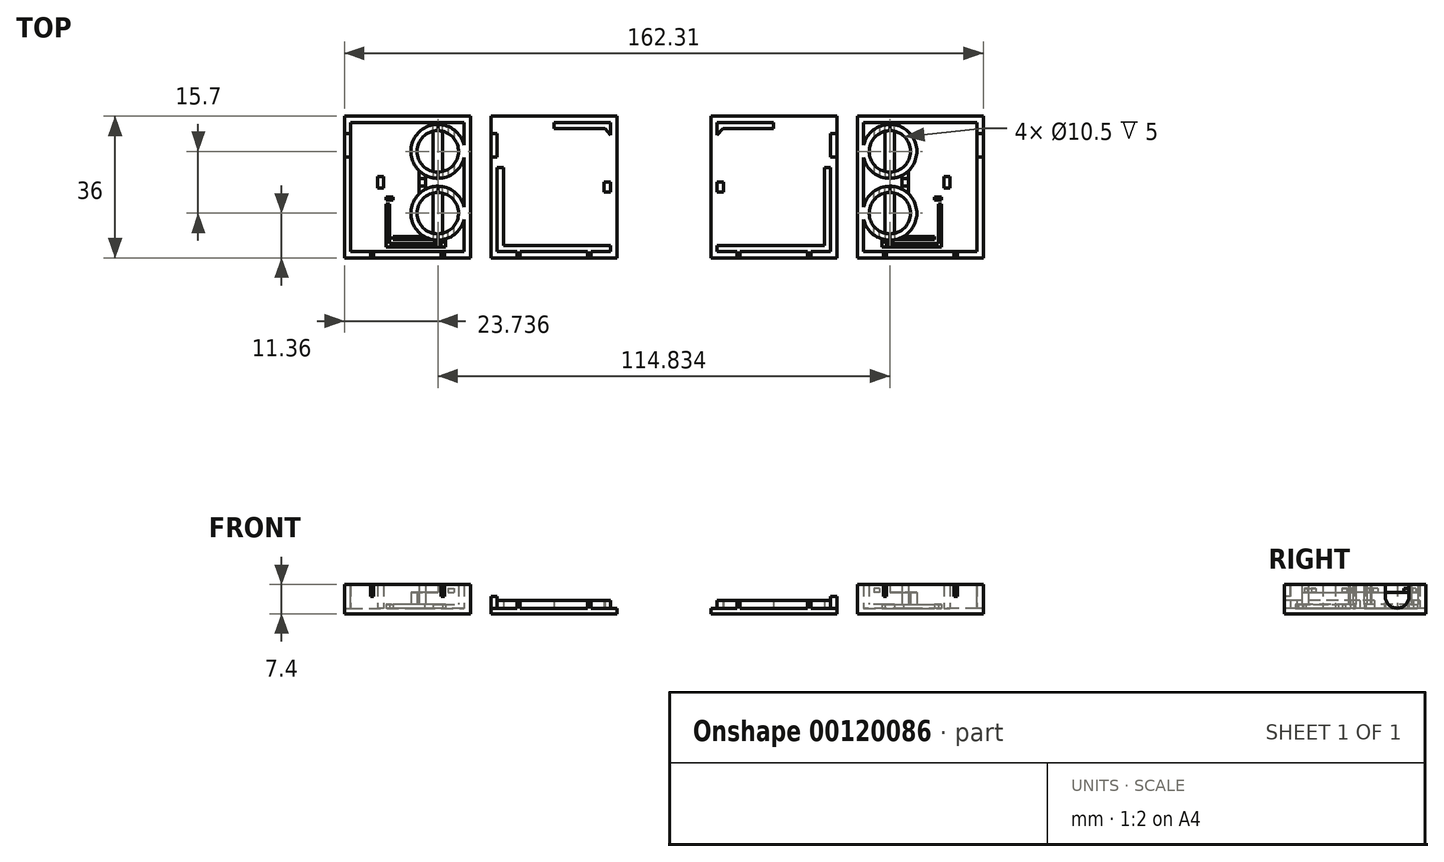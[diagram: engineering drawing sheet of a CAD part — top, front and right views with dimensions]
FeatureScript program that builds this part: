
annotation { "Feature Type Name" : "Feature", "Feature Type Description" : "" }
export const myFeature = defineFeature(function(context is Context, id is Id, definition is map)
    precondition{}
    {
        {
            var Q0;
            Q0=qCreatedBy(makeId("Top.planeOp"),FACE);
            var sketch = newSketch(context, id + "F0", { "sketchPlane" : qUnion([Q0])});
            skLineSegment(sketch, "E0.bottom", {"start": v(-74.61, 24.5) * mm, "end": v(34.71, 24.5) * mm});
            skLineSegment(sketch, "E0.top", {"start": v(-74.61, -26.63) * mm, "end": v(34.71, -26.63) * mm});
            skLineSegment(sketch, "E0.left", {"start": v(-74.61, 24.5) * mm, "end": v(-74.61, -26.63) * mm});
            skLineSegment(sketch, "E0.right", {"start": v(34.71, 24.5) * mm, "end": v(34.71, -26.63) * mm});
            skPoint(sketch, "E1", {"position": v(-57.42, 4.83) * mm});
            skSolve(sketch);
        }
        {
            var Q0;
            Q0=makeQuery(id+"F0.imprint","IMPRINT",FACE,{"disambiguationData":[TD([[makeQuery(id+"F0.imprint","IMPRINT",EDGE,{"derivedFrom":sQuery(id+"F0.wireOp",EDGE,"E0.bottom")}),-1.0]])]});
            extrude(context, id + "F1", {"entities" : qUnion([Q0]), "depth" : 1.4 * mm});
        }
        {
            var Q0;
            Q0=makeQuery(id+"F1.opExtrude","CAP_FACE",FACE,{"disambiguationData":[OSD([sQuery(id+"F0.wireOp",EDGE,"E0.bottom"),sQuery(id+"F0.wireOp",EDGE,"E0.top"),sQuery(id+"F0.wireOp",EDGE,"E0.left"),sQuery(id+"F0.wireOp",EDGE,"E0.right")])],"isStart":false});
            var sketch = newSketch(context, id + "F2", { "sketchPlane" : qUnion([Q0])});
            skPoint(sketch, "E2", {"position": v(0, 12) * mm});
            skCircle(sketch, "E3", {"center": v(0, 12) * mm, "radius": 5.25 * mm});
            skCircle(sketch, "E4", {"center": v(0, 12) * mm, "radius": 6.85 * mm});
            skLineSegment(sketch, "E5", {"start": v(-1.2, 17.11) * mm, "end": v(-1.2, 6.89) * mm});
            skLineSegment(sketch, "E6", {"start": v(-1.2, 17.11) * mm, "end": v(-1.2, 18.74) * mm});
            skLineSegment(sketch, "E7", {"start": v(-1.2, 6.89) * mm, "end": v(-1.2, 5.26) * mm});
            skLineSegment(sketch, "E8", {"start": v(0, -13.27) * mm, "end": v(0, 27.67) * mm, "construction": true});
            skLineSegment(sketch, "E9.MirrorCS", {"start": v(1.2, 17.11) * mm, "end": v(1.2, 18.74) * mm});
            skLineSegment(sketch, "E10.MirrorCS", {"start": v(1.2, 17.11) * mm, "end": v(1.2, 6.89) * mm});
            skLineSegment(sketch, "E11.MirrorCS", {"start": v(1.2, 6.89) * mm, "end": v(1.2, 5.26) * mm});
            skPoint(sketch, "E12", {"position": v(0, -3.7) * mm});
            skCircle(sketch, "E13", {"center": v(0, -3.7) * mm, "radius": 5.25 * mm});
            skCircle(sketch, "E14", {"center": v(0, -3.7) * mm, "radius": 6.85 * mm});
            skLineSegment(sketch, "E15", {"start": v(-1.2, 1.41) * mm, "end": v(-1.2, -8.81) * mm});
            skLineSegment(sketch, "E16", {"start": v(-1.2, 1.41) * mm, "end": v(-1.2, 3.04) * mm});
            skLineSegment(sketch, "E17", {"start": v(-1.2, -8.81) * mm, "end": v(-1.2, -10.44) * mm});
            skLineSegment(sketch, "E18.MirrorCS", {"start": v(1.2, 1.41) * mm, "end": v(1.2, 3.04) * mm});
            skLineSegment(sketch, "E19.MirrorCS", {"start": v(1.2, 1.41) * mm, "end": v(1.2, -8.81) * mm});
            skLineSegment(sketch, "E20.MirrorCS", {"start": v(1.2, -8.81) * mm, "end": v(1.2, -10.44) * mm});
            skPoint(sketch, "E21", {"position": v(0, 5.15) * mm});
            skPoint(sketch, "E22", {"position": v(0, 3.15) * mm});
            skLineSegment(sketch, "E23.bottom", {"start": v(4.73, 7.04) * mm, "end": v(13.73, 7.04) * mm});
            skLineSegment(sketch, "E23.top", {"start": v(4.73, 1.26) * mm, "end": v(13.73, 1.26) * mm});
            skLineSegment(sketch, "E23.left", {"start": v(4.73, 7.04) * mm, "end": v(4.73, 1.26) * mm});
            skLineSegment(sketch, "E23.right", {"start": v(13.73, 7.04) * mm, "end": v(13.73, 1.26) * mm});
            skPoint(sketch, "E24", {"position": v(4.73, 4.15) * mm});
            skPoint(sketch, "E25", {"position": v(0, 4.15) * mm});
            skLineSegment(sketch, "E26", {"start": v(0, 4.15) * mm, "end": v(8.54, 4.15) * mm, "construction": true});
            skLineSegment(sketch, "E27.left", {"start": v(4.73, 6.05) * mm, "end": v(4.73, 2.25) * mm});
            skLineSegment(sketch, "E27.right", {"start": v(3.13, 5.9) * mm, "end": v(3.13, 2.4) * mm});
            skLineSegment(sketch, "E28.bottom", {"start": v(3.13, 5.15) * mm, "end": v(4.73, 5.15) * mm});
            skLineSegment(sketch, "E28.top", {"start": v(3.13, 3.15) * mm, "end": v(4.73, 3.15) * mm});
            skLineSegment(sketch, "E28.left", {"start": v(3.13, 5.15) * mm, "end": v(3.13, 3.15) * mm});
            skLineSegment(sketch, "E28.right", {"start": v(4.73, 5.15) * mm, "end": v(4.73, 3.15) * mm});
            skLineSegment(sketch, "E29.bottom", {"start": v(6.13, 7.04) * mm, "end": v(12.33, 7.04) * mm});
            skLineSegment(sketch, "E29.top", {"start": v(6.13, 7.84) * mm, "end": v(12.33, 7.84) * mm});
            skLineSegment(sketch, "E29.left", {"start": v(6.13, 7.04) * mm, "end": v(6.13, 7.84) * mm});
            skLineSegment(sketch, "E29.right", {"start": v(12.33, 7.04) * mm, "end": v(12.33, 7.84) * mm});
            skLineSegment(sketch, "E30.bottom", {"start": v(13.73, 5.64) * mm, "end": v(15.33, 5.64) * mm});
            skLineSegment(sketch, "E30.top", {"start": v(13.73, 2.66) * mm, "end": v(15.33, 2.66) * mm});
            skLineSegment(sketch, "E30.left", {"start": v(13.73, 5.64) * mm, "end": v(13.73, 2.66) * mm});
            skLineSegment(sketch, "E30.right", {"start": v(15.33, 5.64) * mm, "end": v(15.33, 2.66) * mm});
            skLineSegment(sketch, "E31.bottom", {"start": v(6.13, 1.26) * mm, "end": v(12.33, 1.26) * mm});
            skLineSegment(sketch, "E31.top", {"start": v(6.13, 0.46) * mm, "end": v(12.33, 0.46) * mm});
            skLineSegment(sketch, "E31.left", {"start": v(6.13, 1.26) * mm, "end": v(6.13, 0.46) * mm});
            skLineSegment(sketch, "E31.right", {"start": v(12.33, 1.26) * mm, "end": v(12.33, 0.46) * mm});
            skSolve(sketch);
        }
        {
            var Q0;
            {var subQ0=sQuery(id+"F2.wireOp",EDGE,"E6");Q0=makeQuery(id+"F2.imprint","IMPRINT",FACE,{"disambiguationData":[TD([[makeQuery(id+"F2.imprint","IMPRINT",EDGE,{"derivedFrom":subQ0}),1.0]])]});}
            var Q1;
            {var subQ0=sQuery(id+"F2.wireOp",EDGE,"E6");Q1=makeQuery(id+"F2.imprint","IMPRINT",FACE,{"disambiguationData":[TD([[makeQuery(id+"F2.imprint","IMPRINT",EDGE,{"derivedFrom":subQ0}),-1.0]])]});}
            var Q2;
            {var subQ1=sQuery(id+"F2.wireOp",EDGE,"E9.MirrorCS");Q2=makeQuery(id+"F2.imprint","IMPRINT",FACE,{"disambiguationData":[TD([[makeQuery(id+"F2.imprint","IMPRINT",EDGE,{"derivedFrom":subQ1}),-1.0]])]});}
            var Q3;
            {var subQ0=sQuery(id+"F2.wireOp",EDGE,"E7");Q3=makeQuery(id+"F2.imprint","IMPRINT",FACE,{"disambiguationData":[TD([[makeQuery(id+"F2.imprint","IMPRINT",EDGE,{"derivedFrom":subQ0}),1.0]])]});}
            var Q4;
            {var subQ1=sQuery(id+"F2.wireOp",EDGE,"E18.MirrorCS");Q4=makeQuery(id+"F2.imprint","IMPRINT",FACE,{"disambiguationData":[TD([[makeQuery(id+"F2.imprint","IMPRINT",EDGE,{"derivedFrom":subQ1}),-1.0]])]});}
            var Q5;
            {var subQ0=sQuery(id+"F2.wireOp",EDGE,"E16");Q5=makeQuery(id+"F2.imprint","IMPRINT",FACE,{"disambiguationData":[TD([[makeQuery(id+"F2.imprint","IMPRINT",EDGE,{"derivedFrom":subQ0}),-1.0]])]});}
            var Q6;
            {var subQ0=sQuery(id+"F2.wireOp",EDGE,"E16");Q6=makeQuery(id+"F2.imprint","IMPRINT",FACE,{"disambiguationData":[TD([[makeQuery(id+"F2.imprint","IMPRINT",EDGE,{"derivedFrom":subQ0}),1.0]])]});}
            var Q7;
            {var subQ0=sQuery(id+"F2.wireOp",EDGE,"E17");Q7=makeQuery(id+"F2.imprint","IMPRINT",FACE,{"disambiguationData":[TD([[makeQuery(id+"F2.imprint","IMPRINT",EDGE,{"derivedFrom":subQ0}),1.0]])]});}
            extrude(context, id + "F3", {"entities" : qUnion([Q0, Q1, Q2, Q3, Q4, Q5, Q6, Q7]), "operationType" : NewBodyOperationType.ADD, "depth" : 4 * mm});
        }
        {
            var Q0;
            {var subQ0=sQuery(id+"F2.wireOp",EDGE,"E6");Q0=makeQuery(id+"F2.imprint","IMPRINT",FACE,{"disambiguationData":[TD([[makeQuery(id+"F2.imprint","IMPRINT",EDGE,{"derivedFrom":subQ0}),-1.0]])]});}
            var Q1;
            {var subQ0=sQuery(id+"F2.wireOp",EDGE,"E7");Q1=makeQuery(id+"F2.imprint","IMPRINT",FACE,{"disambiguationData":[TD([[makeQuery(id+"F2.imprint","IMPRINT",EDGE,{"derivedFrom":subQ0}),1.0]])]});}
            var Q2;
            {var subQ0=sQuery(id+"F2.wireOp",EDGE,"E16");Q2=makeQuery(id+"F2.imprint","IMPRINT",FACE,{"disambiguationData":[TD([[makeQuery(id+"F2.imprint","IMPRINT",EDGE,{"derivedFrom":subQ0}),-1.0]])]});}
            var Q3;
            {var subQ0=sQuery(id+"F2.wireOp",EDGE,"E17");Q3=makeQuery(id+"F2.imprint","IMPRINT",FACE,{"disambiguationData":[TD([[makeQuery(id+"F2.imprint","IMPRINT",EDGE,{"derivedFrom":subQ0}),1.0]])]});}
            var Q4;
            {var subQ3=sQuery(id+"F2.wireOp",EDGE,"E28.bottom");Q4=makeQuery(id+"F2.imprint","IMPRINT",FACE,{"disambiguationData":[TD([[makeQuery(id+"F2.imprint","IMPRINT",EDGE,{"derivedFrom":subQ3}),1.0]])]});}
            var Q5;
            {var subQ3=sQuery(id+"F2.wireOp",EDGE,"E28.top");Q5=makeQuery(id+"F2.imprint","IMPRINT",FACE,{"disambiguationData":[TD([[makeQuery(id+"F2.imprint","IMPRINT",EDGE,{"derivedFrom":subQ3}),-1.0]])]});}
            extrude(context, id + "F4", {"entities" : qUnion([Q0, Q1, Q2, Q3, Q4, Q5]), "operationType" : NewBodyOperationType.REMOVE, "depth" : 1 * mm});
        }
        {
            var Q0;
            {var subQ0=sQuery(id+"F2.wireOp",EDGE,"E5");Q0=makeQuery(id+"F2.imprint","IMPRINT",FACE,{"disambiguationData":[TD([[makeQuery(id+"F2.imprint","IMPRINT",EDGE,{"derivedFrom":subQ0}),-1.0]])]});}
            var Q1;
            {var subQ0=sQuery(id+"F2.wireOp",EDGE,"E10.MirrorCS");Q1=makeQuery(id+"F2.imprint","IMPRINT",FACE,{"disambiguationData":[TD([[makeQuery(id+"F2.imprint","IMPRINT",EDGE,{"derivedFrom":subQ0}),1.0]])]});}
            var Q2;
            {var subQ0=sQuery(id+"F2.wireOp",EDGE,"E15");Q2=makeQuery(id+"F2.imprint","IMPRINT",FACE,{"disambiguationData":[TD([[makeQuery(id+"F2.imprint","IMPRINT",EDGE,{"derivedFrom":subQ0}),-1.0]])]});}
            var Q3;
            {var subQ0=sQuery(id+"F2.wireOp",EDGE,"E19.MirrorCS");Q3=makeQuery(id+"F2.imprint","IMPRINT",FACE,{"disambiguationData":[TD([[makeQuery(id+"F2.imprint","IMPRINT",EDGE,{"derivedFrom":subQ0}),1.0]])]});}
            extrude(context, id + "F5", {"entities" : qUnion([Q0, Q1, Q2, Q3]), "operationType" : NewBodyOperationType.ADD, "depth" : 1 * mm});
        }
        {
            var Q0;
            Q0=makeQuery(id+"F3.opExtrude","CAP_FACE",FACE,{"disambiguationData":[OSD([sQuery(id+"F2.wireOp",EDGE,"E3"),sQuery(id+"F2.wireOp",EDGE,"E4")])],"isStart":false});
            var sketch = newSketch(context, id + "F6", { "sketchPlane" : qUnion([Q0])});
            skCircle(sketch, "E32.0", {"center": v(0, 12) * mm, "radius": 6.85 * mm});
            skCircle(sketch, "E32.1", {"center": v(0, 12) * mm, "radius": 5.25 * mm});
            skLineSegment(sketch, "E33", {"start": v(-2.62, 18.33) * mm, "end": v(-2.62, 16.55) * mm});
            skLineSegment(sketch, "E34", {"start": v(-2.62, 7.45) * mm, "end": v(-2.62, 5.67) * mm});
            skLineSegment(sketch, "E35", {"start": v(-4.1, 17.5) * mm, "end": v(-4.1, 15.3) * mm});
            skLineSegment(sketch, "E36", {"start": v(-4.1, 8.7) * mm, "end": v(-4.1, 6.5) * mm});
            skLineSegment(sketch, "E37", {"start": v(0, 18.85) * mm, "end": v(0, 17.25) * mm});
            skLineSegment(sketch, "E38", {"start": v(0, 6.75) * mm, "end": v(0, 5.15) * mm});
            skCircle(sketch, "E39.0", {"center": v(0, -3.7) * mm, "radius": 6.85 * mm});
            skPoint(sketch, "E40", {"position": v(0, 3.15) * mm});
            skPoint(sketch, "E41", {"position": v(0, 5.15) * mm});
            skPoint(sketch, "E42", {"position": v(0, 4.15) * mm});
            skLineSegment(sketch, "E43", {"start": v(0, 4.15) * mm, "end": v(2.8, 4.15) * mm, "construction": true});
            skCircle(sketch, "E44.1", {"center": v(0, -3.7) * mm, "radius": 5.25 * mm});
            skLineSegment(sketch, "E45.MirrorCS", {"start": v(0, -10.55) * mm, "end": v(0, -8.95) * mm});
            skLineSegment(sketch, "E46.MirrorCS", {"start": v(0, 1.55) * mm, "end": v(0, 3.15) * mm});
            skLineSegment(sketch, "E47.MirrorCS", {"start": v(-2.62, 0.85) * mm, "end": v(-2.62, 2.63) * mm});
            skLineSegment(sketch, "E48.MirrorCS", {"start": v(-4.1, -0.4) * mm, "end": v(-4.1, 1.8) * mm});
            skLineSegment(sketch, "E49.MirrorCS", {"start": v(-4.1, -9.2) * mm, "end": v(-4.1, -7) * mm});
            skLineSegment(sketch, "E50.MirrorCS", {"start": v(-2.62, -10.03) * mm, "end": v(-2.62, -8.25) * mm});
            skSolve(sketch);
        }
        {
            var Q0;
            {var subQ0=sQuery(id+"F6.wireOp",EDGE,"E34");Q0=makeQuery(id+"F6.imprint","IMPRINT",FACE,{"disambiguationData":[TD([[makeQuery(id+"F6.imprint","IMPRINT",EDGE,{"derivedFrom":subQ0}),-1.0]])]});}
            var Q1;
            {var subQ0=sQuery(id+"F6.wireOp",EDGE,"E34");Q1=makeQuery(id+"F6.imprint","IMPRINT",FACE,{"disambiguationData":[TD([[makeQuery(id+"F6.imprint","IMPRINT",EDGE,{"derivedFrom":subQ0}),1.0]])]});}
            var Q2;
            {var subQ0=sQuery(id+"F6.wireOp",EDGE,"E35");Q2=makeQuery(id+"F6.imprint","IMPRINT",FACE,{"disambiguationData":[TD([[makeQuery(id+"F6.imprint","IMPRINT",EDGE,{"derivedFrom":subQ0}),-1.0]])]});}
            var Q3;
            {var subQ0=sQuery(id+"F6.wireOp",EDGE,"E33");Q3=makeQuery(id+"F6.imprint","IMPRINT",FACE,{"disambiguationData":[TD([[makeQuery(id+"F6.imprint","IMPRINT",EDGE,{"derivedFrom":subQ0}),-1.0]])]});}
            var Q4;
            {var subQ0=sQuery(id+"F6.wireOp",EDGE,"E33");Q4=makeQuery(id+"F6.imprint","IMPRINT",FACE,{"disambiguationData":[TD([[makeQuery(id+"F6.imprint","IMPRINT",EDGE,{"derivedFrom":subQ0}),1.0]])]});}
            var Q5;
            {var subQ0=sQuery(id+"F6.wireOp",EDGE,"E46.MirrorCS");Q5=makeQuery(id+"F6.imprint","IMPRINT",FACE,{"disambiguationData":[TD([[makeQuery(id+"F6.imprint","IMPRINT",EDGE,{"derivedFrom":subQ0}),1.0]])]});}
            var Q6;
            {var subQ0=sQuery(id+"F6.wireOp",EDGE,"e471a65d-4303-4913-abdb-3468ae2621e10.MirrorCS");Q6=makeQuery(id+"F6.imprint","IMPRINT",FACE,{"disambiguationData":[TD([[makeQuery(id+"F6.imprint","IMPRINT",EDGE,{"derivedFrom":subQ0}),-1.0]])]});}
            var Q7;
            {var subQ0=sQuery(id+"F6.wireOp",EDGE,"5b1a3acc-e78c-430d-9cd8-c20c377ed4240.MirrorCS");Q7=makeQuery(id+"F6.imprint","IMPRINT",FACE,{"disambiguationData":[TD([[makeQuery(id+"F6.imprint","IMPRINT",EDGE,{"derivedFrom":subQ0}),1.0]])]});}
            var Q8;
            {var subQ0=sQuery(id+"F6.wireOp",EDGE,"15c0f35e-76e1-4131-a015-eb208204689e0.MirrorCS");Q8=makeQuery(id+"F6.imprint","IMPRINT",FACE,{"disambiguationData":[TD([[makeQuery(id+"F6.imprint","IMPRINT",EDGE,{"derivedFrom":subQ0}),1.0]])]});}
            var Q9;
            {var subQ0=sQuery(id+"F6.wireOp",EDGE,"E45.MirrorCS");Q9=makeQuery(id+"F6.imprint","IMPRINT",FACE,{"disambiguationData":[TD([[makeQuery(id+"F6.imprint","IMPRINT",EDGE,{"derivedFrom":subQ0}),1.0]])]});}
            var Q10;
            {var subQ0=sQuery(id+"F6.wireOp",EDGE,"E47.MirrorCS");Q10=makeQuery(id+"F6.imprint","IMPRINT",FACE,{"disambiguationData":[TD([[makeQuery(id+"F6.imprint","IMPRINT",EDGE,{"derivedFrom":subQ0}),1.0]])]});}
            var Q11;
            {var subQ0=sQuery(id+"F6.wireOp",EDGE,"E48.MirrorCS");Q11=makeQuery(id+"F6.imprint","IMPRINT",FACE,{"disambiguationData":[TD([[makeQuery(id+"F6.imprint","IMPRINT",EDGE,{"derivedFrom":subQ0}),1.0]])]});}
            var Q12;
            {var subQ0=sQuery(id+"F6.wireOp",EDGE,"E49.MirrorCS");Q12=makeQuery(id+"F6.imprint","IMPRINT",FACE,{"disambiguationData":[TD([[makeQuery(id+"F6.imprint","IMPRINT",EDGE,{"derivedFrom":subQ0}),-1.0]])]});}
            extrude(context, id + "F7", {"entities" : qUnion([Q0, Q1, Q2, Q3, Q4, Q5, Q6, Q7, Q8, Q9, Q10, Q11, Q12]), "operationType" : NewBodyOperationType.ADD, "depth" : 2 * mm});
        }
        {
            var Q0;
            {var subQ0=sQuery(id+"F6.wireOp",EDGE,"E47.MirrorCS");Q0=makeQuery(id+"F6.imprint","IMPRINT",FACE,{"disambiguationData":[TD([[makeQuery(id+"F6.imprint","IMPRINT",EDGE,{"derivedFrom":subQ0}),1.0]])]});}
            var Q1;
            {var subQ0=sQuery(id+"F6.wireOp",EDGE,"E33");Q1=makeQuery(id+"F6.imprint","IMPRINT",FACE,{"disambiguationData":[TD([[makeQuery(id+"F6.imprint","IMPRINT",EDGE,{"derivedFrom":subQ0}),-1.0]])]});}
            var Q2;
            {var subQ0=sQuery(id+"F6.wireOp",EDGE,"E34");Q2=makeQuery(id+"F6.imprint","IMPRINT",FACE,{"disambiguationData":[TD([[makeQuery(id+"F6.imprint","IMPRINT",EDGE,{"derivedFrom":subQ0}),-1.0]])]});}
            var Q3;
            {var subQ0=sQuery(id+"F6.wireOp",EDGE,"E49.MirrorCS");Q3=makeQuery(id+"F6.imprint","IMPRINT",FACE,{"disambiguationData":[TD([[makeQuery(id+"F6.imprint","IMPRINT",EDGE,{"derivedFrom":subQ0}),-1.0]])]});}
            extrude(context, id + "F8", {"entities" : qUnion([Q0, Q1, Q2, Q3]), "operationType" : NewBodyOperationType.REMOVE, "depth" : 1 * mm});
        }
        {
            var Q0;
            Q0=makeQuery(id+"F2.imprint","IMPRINT",FACE,{"disambiguationData":[TD([[makeQuery(id+"F2.imprint","IMPRINT",EDGE,{"derivedFrom":sQuery(id+"F2.wireOp",EDGE,"E28.bottom")}),-1.0]])]});
            extrude(context, id + "F9", {"entities" : qUnion([Q0]), "operationType" : NewBodyOperationType.ADD, "depth" : 4 * mm});
        }
        {
            var Q0;
            {var subQ0=sQuery(id+"F2.wireOp",EDGE,"E27.bottom");Q0=makeQuery(id+"F2.imprint","IMPRINT",FACE,{"disambiguationData":[TD([[makeQuery(id+"F2.imprint","IMPRINT",EDGE,{"derivedFrom":subQ0}),1.0]])]});}
            var Q1;
            {var subQ0=sQuery(id+"F2.wireOp",EDGE,"E27.top");Q1=makeQuery(id+"F2.imprint","IMPRINT",FACE,{"disambiguationData":[TD([[makeQuery(id+"F2.imprint","IMPRINT",EDGE,{"derivedFrom":subQ0}),-1.0]])]});}
            var Q2;
            Q2=makeQuery(id+"F2.imprint","IMPRINT",FACE,{"disambiguationData":[TD([[makeQuery(id+"F2.imprint","IMPRINT",EDGE,{"derivedFrom":sQuery(id+"F2.wireOp",EDGE,"E29.bottom")}),1.0]])]});
            var Q3;
            Q3=makeQuery(id+"F2.imprint","IMPRINT",FACE,{"disambiguationData":[TD([[makeQuery(id+"F2.imprint","IMPRINT",EDGE,{"derivedFrom":sQuery(id+"F2.wireOp",EDGE,"E30.bottom")}),-1.0]])]});
            var Q4;
            Q4=makeQuery(id+"F2.imprint","IMPRINT",FACE,{"disambiguationData":[TD([[makeQuery(id+"F2.imprint","IMPRINT",EDGE,{"derivedFrom":sQuery(id+"F2.wireOp",EDGE,"E31.bottom")}),-1.0]])]});
            var Q5;
            {var subQ3=sQuery(id+"F2.wireOp",EDGE,"E28.bottom");Q5=makeQuery(id+"F2.imprint","IMPRINT",FACE,{"disambiguationData":[TD([[makeQuery(id+"F2.imprint","IMPRINT",EDGE,{"derivedFrom":subQ3}),1.0]])]});}
            var Q6;
            {var subQ3=sQuery(id+"F2.wireOp",EDGE,"E28.top");Q6=makeQuery(id+"F2.imprint","IMPRINT",FACE,{"disambiguationData":[TD([[makeQuery(id+"F2.imprint","IMPRINT",EDGE,{"derivedFrom":subQ3}),-1.0]])]});}
            extrude(context, id + "F10", {"entities" : qUnion([Q0, Q1, Q2, Q3, Q4, Q5, Q6]), "operationType" : NewBodyOperationType.ADD, "depth" : 6 * mm});
        }
        {
            var Q0;
            {var subQ0=sQuery(id+"F2.wireOp",EDGE,"E14");var subQ1=sQuery(id+"F2.wireOp",EDGE,"E13");var subQ2=sQuery(id+"F2.wireOp",EDGE,"E4");var subQ3=sQuery(id+"F2.wireOp",EDGE,"E3");var subQ4=sQuery(id+"F0.wireOp",EDGE,"E0.right");var subQ5=sQuery(id+"F0.wireOp",EDGE,"E0.left");var subQ6=sQuery(id+"F0.wireOp",EDGE,"E0.top");var subQ7=sQuery(id+"F0.wireOp",EDGE,"E0.bottom");var subQ8=makeQuery(id+"F1.opExtrude","CAP_FACE",FACE,{"disambiguationData":[OSD([subQ7,subQ6,subQ5,subQ4])],"isStart":false});Q0=makeQuery(id+"F4.boolean.opBoolean","MERGE",FACE,{"derivedFrom":[makeQuery(id+"F3.boolean.opBoolean","SPLIT",FACE,{"disambiguationData":[TD([makeQuery(id+"F1.opExtrude","SWEPT_FACE",FACE,{"disambiguationData":[OSD([subQ7])]})])],"derivedFrom":subQ8}),makeQuery(id+"F3.boolean.opBoolean","SPLIT",FACE,{"disambiguationData":[TD([makeQuery(id+"F3.opExtrude","SWEPT_FACE",FACE,{"disambiguationData":[OSD([subQ3])]})])],"derivedFrom":subQ8}),makeQuery(id+"F3.boolean.opBoolean","SPLIT",FACE,{"disambiguationData":[TD([makeQuery(id+"F3.opExtrude","SWEPT_FACE",FACE,{"disambiguationData":[OSD([subQ1])]})])],"derivedFrom":subQ8}),makeQuery(id+"F4.opExtrude","CAP_FACE",FACE,{"disambiguationData":[OSD([subQ3,subQ2,sQuery(id+"F2.wireOp",EDGE,"E6"),sQuery(id+"F2.wireOp",EDGE,"E9.MirrorCS")])],"isStart":true}),makeQuery(id+"F4.opExtrude","CAP_FACE",FACE,{"disambiguationData":[OSD([subQ3,subQ2,sQuery(id+"F2.wireOp",EDGE,"E7"),sQuery(id+"F2.wireOp",EDGE,"E11.MirrorCS")])],"isStart":true}),makeQuery(id+"F4.opExtrude","CAP_FACE",FACE,{"disambiguationData":[OSD([subQ1,subQ0,sQuery(id+"F2.wireOp",EDGE,"E16"),sQuery(id+"F2.wireOp",EDGE,"E18.MirrorCS")])],"isStart":true}),makeQuery(id+"F4.opExtrude","CAP_FACE",FACE,{"disambiguationData":[OSD([subQ1,subQ0,sQuery(id+"F2.wireOp",EDGE,"E17"),sQuery(id+"F2.wireOp",EDGE,"E20.MirrorCS")])],"isStart":true})]});}
            var sketch = newSketch(context, id + "F11", { "sketchPlane" : qUnion([Q0])});
            skCircle(sketch, "E51.0", {"center": v(0, -3.7) * mm, "radius": 6.85 * mm});
            skLineSegment(sketch, "E52.bottom", {"start": v(-1.2, -10.44) * mm, "end": v(12.33, -10.44) * mm});
            skLineSegment(sketch, "E52.top", {"start": v(-1.2, -11.44) * mm, "end": v(12.33, -11.44) * mm});
            skLineSegment(sketch, "E52.left", {"start": v(-1.2, -10.44) * mm, "end": v(-1.2, -11.44) * mm});
            skLineSegment(sketch, "E52.right", {"start": v(12.33, -10.44) * mm, "end": v(12.33, -11.44) * mm});
            skLineSegment(sketch, "E53.bottom", {"start": v(12.33, -10.44) * mm, "end": v(11.33, -10.44) * mm});
            skLineSegment(sketch, "E53.top", {"start": v(12.33, 0.46) * mm, "end": v(11.33, 0.46) * mm});
            skLineSegment(sketch, "E53.left", {"start": v(12.33, -10.44) * mm, "end": v(12.33, 0.46) * mm});
            skLineSegment(sketch, "E53.right", {"start": v(11.33, -10.44) * mm, "end": v(11.33, 0.46) * mm});
            skLineSegment(sketch, "E54.bottom", {"start": v(11.33, -1.34) * mm, "end": v(22.04, -1.34) * mm});
            skLineSegment(sketch, "E54.top", {"start": v(11.33, -0.34) * mm, "end": v(22.04, -0.34) * mm});
            skLineSegment(sketch, "E54.left", {"start": v(11.33, -1.34) * mm, "end": v(11.33, -0.34) * mm});
            skLineSegment(sketch, "E54.right", {"start": v(22.04, -1.34) * mm, "end": v(22.04, -0.34) * mm});
            skPoint(sketch, "E55", {"position": v(12.33, -0.34) * mm});
            skPoint(sketch, "E56", {"position": v(12.33, -1.34) * mm});
            skLineSegment(sketch, "E57.bottom", {"start": v(-2, -9.64) * mm, "end": v(13.13, -9.64) * mm});
            skLineSegment(sketch, "E57.top", {"start": v(-2, -12.24) * mm, "end": v(13.13, -12.24) * mm});
            skLineSegment(sketch, "E57.left", {"start": v(-2, -9.64) * mm, "end": v(-2, -12.24) * mm});
            skLineSegment(sketch, "E57.right", {"start": v(13.13, -9.64) * mm, "end": v(13.13, -12.24) * mm});
            skLineSegment(sketch, "E58.bottom", {"start": v(13.13, -9.64) * mm, "end": v(10.53, -9.64) * mm});
            skLineSegment(sketch, "E58.top", {"start": v(13.13, 0.46) * mm, "end": v(10.53, 0.46) * mm});
            skLineSegment(sketch, "E58.left", {"start": v(13.13, -9.64) * mm, "end": v(13.13, 0.46) * mm});
            skLineSegment(sketch, "E58.right", {"start": v(10.53, -9.64) * mm, "end": v(10.53, 0.46) * mm});
            skLineSegment(sketch, "E59.bottom", {"start": v(13.13, 0.46) * mm, "end": v(21.62, 0.46) * mm});
            skLineSegment(sketch, "E59.top", {"start": v(13.13, -2.14) * mm, "end": v(21.62, -2.14) * mm});
            skLineSegment(sketch, "E59.left", {"start": v(13.13, 0.46) * mm, "end": v(13.13, -2.14) * mm});
            skLineSegment(sketch, "E59.right", {"start": v(21.62, 0.46) * mm, "end": v(21.62, -2.14) * mm});
            skPoint(sketch, "E60", {"position": v(3.4, -9.64) * mm});
            skPoint(sketch, "E61", {"position": v(-2, -10.25) * mm});
            skPoint(sketch, "E62", {"position": v(-1.2, -10.44) * mm});
            skLineSegment(sketch, "E63.bottom", {"start": v(6.8, 19.34) * mm, "end": v(22.14, 19.34) * mm});
            skLineSegment(sketch, "E63.top", {"start": v(6.8, 7.84) * mm, "end": v(22.14, 7.84) * mm});
            skLineSegment(sketch, "E63.left", {"start": v(6.8, 11.2) * mm, "end": v(6.8, 7.84) * mm});
            skLineSegment(sketch, "E63.right", {"start": v(22.14, 19.34) * mm, "end": v(22.14, 7.84) * mm});
            skLineSegment(sketch, "E64", {"start": v(6.8, 19.34) * mm, "end": v(6.8, 11.2) * mm});
            skLineSegment(sketch, "E65", {"start": v(22.14, 7.84) * mm, "end": v(22.14, -11.25) * mm});
            skLineSegment(sketch, "E66.bottom", {"start": v(22.14, 19.34) * mm, "end": v(-6.66, 19.34) * mm});
            skLineSegment(sketch, "E66.top", {"start": v(22.14, -13.46) * mm, "end": v(-6.66, -13.46) * mm});
            skLineSegment(sketch, "E66.left", {"start": v(22.14, 19.34) * mm, "end": v(22.14, -13.46) * mm});
            skLineSegment(sketch, "E66.right", {"start": v(-6.66, 19.34) * mm, "end": v(-6.66, -13.46) * mm});
            skLineSegment(sketch, "E67.bottom", {"start": v(23.74, -15.06) * mm, "end": v(-8.26, -15.06) * mm});
            skLineSegment(sketch, "E67.top", {"start": v(23.74, 20.94) * mm, "end": v(-8.26, 20.94) * mm});
            skLineSegment(sketch, "E67.left", {"start": v(23.74, -15.06) * mm, "end": v(23.74, 20.94) * mm});
            skLineSegment(sketch, "E67.right", {"start": v(-8.26, -15.06) * mm, "end": v(-8.26, 20.94) * mm});
            skLineSegment(sketch, "E68.bottom", {"start": v(-13.46, 20.94) * mm, "end": v(-45.46, 20.94) * mm});
            skLineSegment(sketch, "E68.top", {"start": v(-13.46, -15.06) * mm, "end": v(-45.46, -15.06) * mm});
            skLineSegment(sketch, "E68.left", {"start": v(-13.46, 20.94) * mm, "end": v(-13.46, -15.06) * mm});
            skLineSegment(sketch, "E68.right", {"start": v(-45.46, 20.94) * mm, "end": v(-45.46, -15.06) * mm});
            skLineSegment(sketch, "E69.bottom", {"start": v(-43.86, 19.34) * mm, "end": v(-15.06, 19.34) * mm});
            skLineSegment(sketch, "E69.top", {"start": v(-43.86, -13.46) * mm, "end": v(-15.06, -13.46) * mm});
            skLineSegment(sketch, "E69.left", {"start": v(-43.86, 19.34) * mm, "end": v(-43.86, -13.46) * mm});
            skLineSegment(sketch, "E69.right", {"start": v(-15.06, 19.34) * mm, "end": v(-15.06, -13.46) * mm});
            skLineSegment(sketch, "E70", {"start": v(-43.86, 16.14) * mm, "end": v(-41.03, 19.34) * mm});
            skPoint(sketch, "E71.firstSnap0", {"position": v(3.13, 4.15) * mm});
            skLineSegment(sketch, "E71.bottom", {"start": v(-43.86, 4.15) * mm, "end": v(-42.26, 4.15) * mm});
            skLineSegment(sketch, "E71.top", {"start": v(-43.86, 1.65) * mm, "end": v(-42.26, 1.65) * mm});
            skLineSegment(sketch, "E71.left", {"start": v(-43.86, 4.15) * mm, "end": v(-43.86, 1.65) * mm});
            skLineSegment(sketch, "E71.right", {"start": v(-42.26, 4.15) * mm, "end": v(-42.26, 1.65) * mm});
            skLineSegment(sketch, "E72.bottom", {"start": v(-42.26, 4.15) * mm, "end": v(-43.86, 4.15) * mm});
            skLineSegment(sketch, "E72.top", {"start": v(-42.26, 6.65) * mm, "end": v(-43.86, 6.65) * mm});
            skLineSegment(sketch, "E72.left", {"start": v(-42.26, 4.15) * mm, "end": v(-42.26, 6.65) * mm});
            skLineSegment(sketch, "E72.right", {"start": v(-43.86, 4.15) * mm, "end": v(-43.86, 6.65) * mm});
            skLineSegment(sketch, "E73", {"start": v(-43.86, -11.86) * mm, "end": v(-15.06, -11.86) * mm});
            skPoint(sketch, "E74", {"position": v(-15.06, 7.84) * mm});
            skLineSegment(sketch, "E75.bottom", {"start": v(-15.06, 7.84) * mm, "end": v(-16.66, 7.84) * mm});
            skLineSegment(sketch, "E75.top", {"start": v(-15.06, -11.86) * mm, "end": v(-16.66, -11.86) * mm});
            skLineSegment(sketch, "E75.left", {"start": v(-15.06, 7.84) * mm, "end": v(-15.06, -11.86) * mm});
            skLineSegment(sketch, "E75.right", {"start": v(-16.66, 7.84) * mm, "end": v(-16.66, -11.86) * mm});
            skPoint(sketch, "E76", {"position": v(-15.06, 19.34) * mm});
            skPoint(sketch, "E77", {"position": v(-29.56, 19.34) * mm});
            skLineSegment(sketch, "E78.bottom", {"start": v(-29.56, 19.34) * mm, "end": v(-42.45, 19.34) * mm});
            skLineSegment(sketch, "E78.top", {"start": v(-29.56, 17.74) * mm, "end": v(-42.45, 17.74) * mm});
            skLineSegment(sketch, "E78.left", {"start": v(-29.56, 19.34) * mm, "end": v(-29.56, 17.74) * mm});
            skLineSegment(sketch, "E78.right", {"start": v(-42.45, 19.34) * mm, "end": v(-42.45, 17.74) * mm});
            skPoint(sketch, "E79", {"position": v(-38.86, -13.46) * mm});
            skPoint(sketch, "E80", {"position": v(-38.06, -13.46) * mm});
            skPoint(sketch, "E81", {"position": v(-20.06, -13.46) * mm});
            skPoint(sketch, "E82", {"position": v(-20.86, -13.46) * mm});
            skLineSegment(sketch, "E83", {"start": v(-38.86, -13.46) * mm, "end": v(-38.86, -15.06) * mm});
            skLineSegment(sketch, "E84", {"start": v(-38.06, -13.46) * mm, "end": v(-38.06, -15.06) * mm});
            skLineSegment(sketch, "E85", {"start": v(-20.86, -13.46) * mm, "end": v(-20.86, -15.06) * mm});
            skLineSegment(sketch, "E86", {"start": v(-20.06, -13.46) * mm, "end": v(-20.06, -15.06) * mm});
            skPoint(sketch, "E87", {"position": v(-15.06, 13.6) * mm});
            skLineSegment(sketch, "E88", {"start": v(-15.06, 16.6) * mm, "end": v(-13.46, 16.6) * mm});
            skLineSegment(sketch, "E89", {"start": v(-15.06, 10.6) * mm, "end": v(-13.46, 10.6) * mm});
            skPoint(sketch, "E90.0", {"position": v(1.2, -10.44) * mm});
            skSolve(sketch);
        }
        {
            var Q0;
            {var subQ1=sQuery(id+"F11.wireOp",EDGE,"E52.bottom");var subQ7=sQuery(id+"F11.wireOp",EDGE,"E51.0");var subQ9=makeQuery(id+"F11.imprint","INTERSECT",VERTEX,{"derivedFrom":[subQ7,subQ1]});Q0=makeQuery(id+"F11.imprint","IMPRINT",FACE,{"disambiguationData":[TD([[makeQuery(id+"F11.imprint","IMPRINT",EDGE,{"disambiguationData":[TD([[subQ9,-1.0]])],"derivedFrom":subQ7}),-1.0]])]});}
            var Q1;
            {var subQ4=sQuery(id+"F11.wireOp",EDGE,"E54.left");Q1=makeQuery(id+"F11.imprint","IMPRINT",FACE,{"disambiguationData":[TD([[makeQuery(id+"F11.imprint","IMPRINT",EDGE,{"derivedFrom":subQ4}),1.0]])]});}
            var Q2;
            {var subQ0=sQuery(id+"F11.wireOp",EDGE,"E58.left");Q2=makeQuery(id+"F11.imprint","IMPRINT",FACE,{"disambiguationData":[TD([[makeQuery(id+"F11.imprint","IMPRINT",EDGE,{"derivedFrom":subQ0}),1.0]])]});}
            var Q3;
            {var subQ0=sQuery(id+"F11.wireOp",EDGE,"E58.top");var subQ1=sQuery(id+"F11.wireOp",EDGE,"E53.left");var subQ2=makeQuery(id+"F11.imprint","INTERSECT",VERTEX,{"derivedFrom":[subQ1,subQ0]});Q3=makeQuery(id+"F11.imprint","IMPRINT",FACE,{"disambiguationData":[TD([[makeQuery(id+"F11.imprint","IMPRINT",EDGE,{"disambiguationData":[TD([[subQ2,1.0]])],"derivedFrom":subQ1}),-1.0]])]});}
            var Q4;
            {var subQ0=sQuery(id+"F11.wireOp",EDGE,"E58.top");var subQ1=sQuery(id+"F11.wireOp",EDGE,"E53.left");var subQ2=makeQuery(id+"F11.imprint","INTERSECT",VERTEX,{"derivedFrom":[subQ1,subQ0]});Q4=makeQuery(id+"F11.imprint","IMPRINT",FACE,{"disambiguationData":[TD([[makeQuery(id+"F11.imprint","IMPRINT",EDGE,{"disambiguationData":[TD([[subQ2,1.0]])],"derivedFrom":subQ1}),1.0]])]});}
            var Q5;
            {var subQ5=sQuery(id+"F11.wireOp",EDGE,"E52.top");Q5=makeQuery(id+"F11.imprint","IMPRINT",FACE,{"disambiguationData":[TD([[makeQuery(id+"F11.imprint","IMPRINT",EDGE,{"derivedFrom":subQ5}),-1.0]])]});}
            extrude(context, id + "F12", {"entities" : qUnion([Q0, Q1, Q2, Q3, Q4, Q5]), "operationType" : NewBodyOperationType.ADD, "depth" : 1 * mm});
        }
        {
            var Q0;
            {var subQ2=sQuery(id+"F11.wireOp",EDGE,"E66.top");Q0=makeQuery(id+"F11.imprint","IMPRINT",FACE,{"disambiguationData":[TD([[makeQuery(id+"F11.imprint","IMPRINT",EDGE,{"derivedFrom":subQ2}),1.0]])]});}
            extrude(context, id + "F13", {"entities" : qUnion([Q0]), "operationType" : NewBodyOperationType.ADD, "depth" : 6 * mm});
        }
        {
            var Q0;
            Q0=makeQuery(id+"F13.opExtrude","SWEPT_FACE",FACE,{"disambiguationData":[OSD([sQuery(id+"F11.wireOp",EDGE,"E66.left")])]});
            var sketch = newSketch(context, id + "F14", { "sketchPlane" : qUnion([Q0])});
            skPoint(sketch, "E91.0", {"position": v(-7.84, 1.4) * mm});
            skPoint(sketch, "E91.1", {"position": v(-19.34, 1.4) * mm});
            skLineSegment(sketch, "E92.1", {"start": v(-19.34, 1.4) * mm, "end": v(13.46, 1.4) * mm});
            skPoint(sketch, "E93", {"position": v(-13.6, 1.4) * mm});
            skLineSegment(sketch, "E94", {"start": v(-13.6, 1.4) * mm, "end": v(-13.6, 7.4) * mm});
            skPoint(sketch, "E95", {"position": v(-13.6, 4.4) * mm});
            skCircle(sketch, "E96", {"center": v(-13.6, 4.4) * mm, "radius": 3 * mm});
            skLineSegment(sketch, "E97", {"start": v(-16.6, 4.4) * mm, "end": v(-16.6, 7.4) * mm});
            skLineSegment(sketch, "E98", {"start": v(-10.6, 4.4) * mm, "end": v(-10.6, 7.4) * mm});
            skSolve(sketch);
        }
        {
            var Q0;
            {var subQ3=sQuery(id+"F14.wireOp",EDGE,"E97");Q0=makeQuery(id+"F14.imprint","IMPRINT",FACE,{"disambiguationData":[TD([[makeQuery(id+"F14.imprint","IMPRINT",EDGE,{"derivedFrom":subQ3}),-1.0]])]});}
            var Q1;
            {var subQ0=sQuery(id+"F14.wireOp",EDGE,"E94");Q1=makeQuery(id+"F14.imprint","IMPRINT",FACE,{"disambiguationData":[TD([[makeQuery(id+"F14.imprint","IMPRINT",EDGE,{"derivedFrom":subQ0}),1.0]])]});}
            var Q2;
            {var subQ0=sQuery(id+"F14.wireOp",EDGE,"E94");Q2=makeQuery(id+"F14.imprint","IMPRINT",FACE,{"disambiguationData":[TD([[makeQuery(id+"F14.imprint","IMPRINT",EDGE,{"derivedFrom":subQ0}),-1.0]])]});}
            var Q3;
            {var subQ3=sQuery(id+"F14.wireOp",EDGE,"E98");Q3=makeQuery(id+"F14.imprint","IMPRINT",FACE,{"disambiguationData":[TD([[makeQuery(id+"F14.imprint","IMPRINT",EDGE,{"derivedFrom":subQ3}),1.0]])]});}
            extrude(context, id + "F15", {"entities" : qUnion([Q0, Q1, Q2, Q3]), "operationType" : NewBodyOperationType.REMOVE, "oppositeDirection" : true, "depth" : 2 * mm});
        }
        {
            var Q0;
            Q0=makeQuery(id+"F13.opExtrude","CAP_FACE",FACE,{"disambiguationData":[OSD([sQuery(id+"F11.wireOp",EDGE,"E66.bottom"),sQuery(id+"F11.wireOp",EDGE,"E66.top"),sQuery(id+"F11.wireOp",EDGE,"E66.left"),sQuery(id+"F11.wireOp",EDGE,"E66.right"),sQuery(id+"F11.wireOp",EDGE,"E67.bottom"),sQuery(id+"F11.wireOp",EDGE,"E67.top"),sQuery(id+"F11.wireOp",EDGE,"E67.left"),sQuery(id+"F11.wireOp",EDGE,"E67.right")])],"isStart":false});
            var sketch = newSketch(context, id + "F16", { "sketchPlane" : qUnion([Q0])});
            skPoint(sketch, "E99", {"position": v(-1.66, -13.46) * mm});
            skPoint(sketch, "E100", {"position": v(-0.86, -13.46) * mm});
            skPoint(sketch, "E101", {"position": v(17.14, -13.46) * mm});
            skPoint(sketch, "E102", {"position": v(16.34, -13.46) * mm});
            skLineSegment(sketch, "E103", {"start": v(-1.66, -13.46) * mm, "end": v(-1.66, -15.06) * mm});
            skLineSegment(sketch, "E104", {"start": v(-0.86, -13.46) * mm, "end": v(-0.86, -15.06) * mm});
            skLineSegment(sketch, "E105", {"start": v(16.34, -13.46) * mm, "end": v(16.34, -15.06) * mm});
            skLineSegment(sketch, "E106", {"start": v(17.14, -13.46) * mm, "end": v(17.14, -15.06) * mm});
            skSolve(sketch);
        }
        {
            var Q0;
            {var subQ0=sQuery(id+"F16.wireOp",EDGE,"E103");Q0=makeQuery(id+"F16.imprint","IMPRINT",FACE,{"disambiguationData":[TD([[makeQuery(id+"F16.imprint","IMPRINT",EDGE,{"derivedFrom":subQ0}),1.0]])]});}
            var Q1;
            {var subQ5=sQuery(id+"F16.wireOp",EDGE,"E106");Q1=makeQuery(id+"F16.imprint","IMPRINT",FACE,{"disambiguationData":[TD([[makeQuery(id+"F16.imprint","IMPRINT",EDGE,{"derivedFrom":subQ5}),-1.0]])]});}
            extrude(context, id + "F17", {"entities" : qUnion([Q0, Q1]), "operationType" : NewBodyOperationType.REMOVE, "oppositeDirection" : true, "depth" : 3 * mm});
        }
        {
            var Q0;
            {var subQ0=sQuery(id+"F11.wireOp",EDGE,"E88");Q0=makeQuery(id+"F11.imprint","IMPRINT",FACE,{"disambiguationData":[TD([[makeQuery(id+"F11.imprint","IMPRINT",EDGE,{"derivedFrom":subQ0}),-1.0]])]});}
            extrude(context, id + "F18", {"entities" : qUnion([Q0]), "operationType" : NewBodyOperationType.ADD, "depth" : 3 * mm});
        }
        {
            var Q0;
            Q0=makeQuery(id+"F18.opExtrude","SWEPT_FACE",FACE,{"disambiguationData":[OSD([sQuery(id+"F11.wireOp",EDGE,"E69.right")])]});
            var sketch = newSketch(context, id + "F19", { "sketchPlane" : qUnion([Q0])});
            skPoint(sketch, "E107", {"position": v(-13.6, 4.4) * mm});
            skCircle(sketch, "E108", {"center": v(-13.6, 4.4) * mm, "radius": 3 * mm});
            skSolve(sketch);
        }
        {
            var Q0;
            Q0 = qSketchRegion(id + "F19", true);
            extrude(context, id + "F20", {"entities" : qUnion([Q0]), "operationType" : NewBodyOperationType.REMOVE, "oppositeDirection" : true, "depth" : 2 * mm});
        }
        {
            var Q0;
            Q0=makeQuery(id+"F11.imprint","IMPRINT",FACE,{"disambiguationData":[TD([[makeQuery(id+"F11.imprint","IMPRINT",EDGE,{"derivedFrom":sQuery(id+"F11.wireOp",EDGE,"E75.bottom")}),1.0]])]});
            var Q1;
            {var subQ3=sQuery(id+"F11.wireOp",EDGE,"E78.top");Q1=makeQuery(id+"F11.imprint","IMPRINT",FACE,{"disambiguationData":[TD([[makeQuery(id+"F11.imprint","IMPRINT",EDGE,{"derivedFrom":subQ3}),-1.0]])]});}
            var Q2;
            {var subQ9=sQuery(id+"F11.wireOp",EDGE,"E73");Q2=makeQuery(id+"F11.imprint","IMPRINT",FACE,{"disambiguationData":[TD([[makeQuery(id+"F11.imprint","IMPRINT",EDGE,{"derivedFrom":subQ9}),-1.0]])]});}
            var Q3;
            {var subQ3=sQuery(id+"F11.wireOp",EDGE,"E78.right");Q3=makeQuery(id+"F11.imprint","IMPRINT",FACE,{"disambiguationData":[TD([[makeQuery(id+"F11.imprint","IMPRINT",EDGE,{"derivedFrom":subQ3}),-1.0]])]});}
            var Q4;
            {var subQ3=sQuery(id+"F11.wireOp",EDGE,"E78.right");Q4=makeQuery(id+"F11.imprint","IMPRINT",FACE,{"disambiguationData":[TD([[makeQuery(id+"F11.imprint","IMPRINT",EDGE,{"derivedFrom":subQ3}),1.0]])]});}
            var Q5;
            Q5=makeQuery(id+"F11.imprint","IMPRINT",FACE,{"disambiguationData":[TD([[makeQuery(id+"F11.imprint","IMPRINT",EDGE,{"derivedFrom":sQuery(id+"F11.wireOp",EDGE,"E72.bottom")}),-1.0]])]});
            var Q6;
            Q6=makeQuery(id+"F11.imprint","IMPRINT",FACE,{"disambiguationData":[TD([[makeQuery(id+"F11.imprint","IMPRINT",EDGE,{"derivedFrom":sQuery(id+"F11.wireOp",EDGE,"E71.top")}),1.0]])]});
            var Q7;
            {var subQ0=sQuery(id+"F11.wireOp",EDGE,"E83");Q7=makeQuery(id+"F11.imprint","IMPRINT",FACE,{"disambiguationData":[TD([[makeQuery(id+"F11.imprint","IMPRINT",EDGE,{"derivedFrom":subQ0}),1.0]])]});}
            var Q8;
            {var subQ0=sQuery(id+"F11.wireOp",EDGE,"E85");Q8=makeQuery(id+"F11.imprint","IMPRINT",FACE,{"disambiguationData":[TD([[makeQuery(id+"F11.imprint","IMPRINT",EDGE,{"derivedFrom":subQ0}),1.0]])]});}
            extrude(context, id + "F21", {"entities" : qUnion([Q0, Q1, Q2, Q3, Q4, Q5, Q6, Q7, Q8]), "operationType" : NewBodyOperationType.ADD, "depth" : 2 * mm});
        }
        {
            var Q0;
            Q0=makeQuery(id+"F11.imprint","IMPRINT",FACE,{"disambiguationData":[TD([[makeQuery(id+"F11.imprint","IMPRINT",EDGE,{"derivedFrom":sQuery(id+"F11.wireOp",EDGE,"E67.bottom")}),1.0]])]});
            extrude(context, id + "F22", {"entities" : qUnion([Q0]), "operationType" : NewBodyOperationType.REMOVE, "oppositeDirection" : true, "depth" : 25 * mm});
        }
        {
            var Q0;
            Q0=sQuery(id+"F0.wireOp",VERTEX,"E1");
            var Q1;
            Q1=qCreatedBy(makeId("Right.planeOp"),FACE);
            cPlane(context, id + "F23", {"entities" : qUnion([Q0, Q1]), "cplaneType" : CPlaneType.PLANE_POINT, "offset" : 25 * mm, "width" : 150 * mm, "height" : 150 * mm});
        }
        {
            var Q0;
            Q0=makeQuery(id+"F22.boolean.opBoolean","SPLIT",BODY,{"disambiguationData":[OD(1.0)],"derivedFrom":makeQuery(id+"F1.opExtrude","SWEPT_BODY",BODY,{"disambiguationData":[OSD([sQuery(id+"F0.wireOp",EDGE,"E0.bottom"),sQuery(id+"F0.wireOp",EDGE,"E0.top"),sQuery(id+"F0.wireOp",EDGE,"E0.left"),sQuery(id+"F0.wireOp",EDGE,"E0.right")])]})});
            var Q1;
            Q1=qCreatedBy(id+"F23.planeOp",FACE);
            mirror(context, id + "F24", {"entities" : qUnion([Q0]), "mirrorPlane" : qUnion([Q1])});
        }
    });
